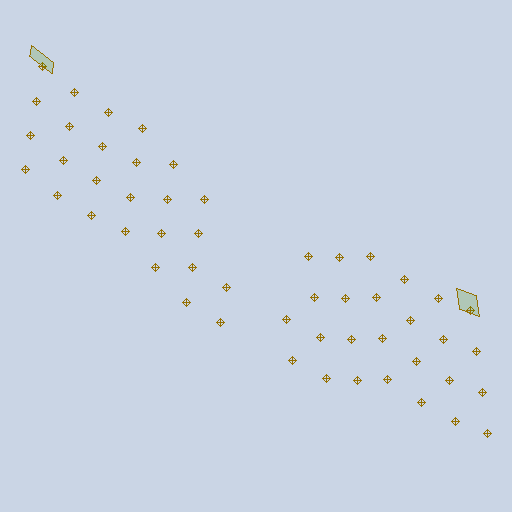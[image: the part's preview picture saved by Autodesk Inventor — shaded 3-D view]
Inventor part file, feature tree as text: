
AUTODESK INVENTOR PART (.ipt)
format: ipt  version: 2023 (Build 270158000, 158)  size: 168,960 bytes
history: native  units: mm
features: other x56, sketch x4, plane x2
ambient origin geometry x8: Origin, YZ Plane, XZ Plane, XY Plane, X Axis, Y Axis, Z Axis, Center Point
feature tree (62):
  plane  "Work Plane1"
  sketch  "Sketch1"
  other  "Work Point1"
  sketch  "Sketch Driven Pattern1"
  plane  "Work Plane2"
  sketch  "Sketch2"
  other  "Work Point27"
  sketch  "Sketch Driven Pattern2"
  other  "Work Point2"
  other  "Work Point3"
  other  "Work Point4"
  other  "Work Point5"
  other  "Work Point6"
  other  "Work Point7"
  other  "Work Point8"
  other  "Work Point9"
  other  "Work Point10"
  other  "Work Point11"
  other  "Work Point12"
  other  "Work Point13"
  other  "Work Point14"
  other  "Work Point15"
  other  "Work Point16"
  other  "Work Point17"
  other  "Work Point18"
  other  "Work Point19"
  other  "Work Point20"
  other  "Work Point21"
  other  "Work Point22"
  other  "Work Point23"
  other  "Work Point24"
  other  "Work Point25"
  other  "Work Point26"
  other  "Work Point28"
  other  "Work Point29"
  other  "Work Point30"
  other  "Work Point31"
  other  "Work Point32"
  other  "Work Point33"
  other  "Work Point34"
  other  "Work Point35"
  other  "Work Point36"
  other  "Work Point37"
  other  "Work Point38"
  other  "Work Point39"
  other  "Work Point40"
  other  "Work Point41"
  other  "Work Point42"
  other  "Work Point43"
  other  "Work Point44"
  other  "Work Point45"
  other  "Work Point46"
  other  "Work Point47"
  other  "Work Point48"
  other  "Work Point49"
  other  "Work Point50"
  other  "Work Point51"
  other  "Work Point52"
  other  "<userpath>\Documents\Inventor\atreus-52\Assembly.iam"
  other  "Assembly.iam"
  other  "Kailh Hotswap:1"
  other  "Kailh Hotswap:27"
